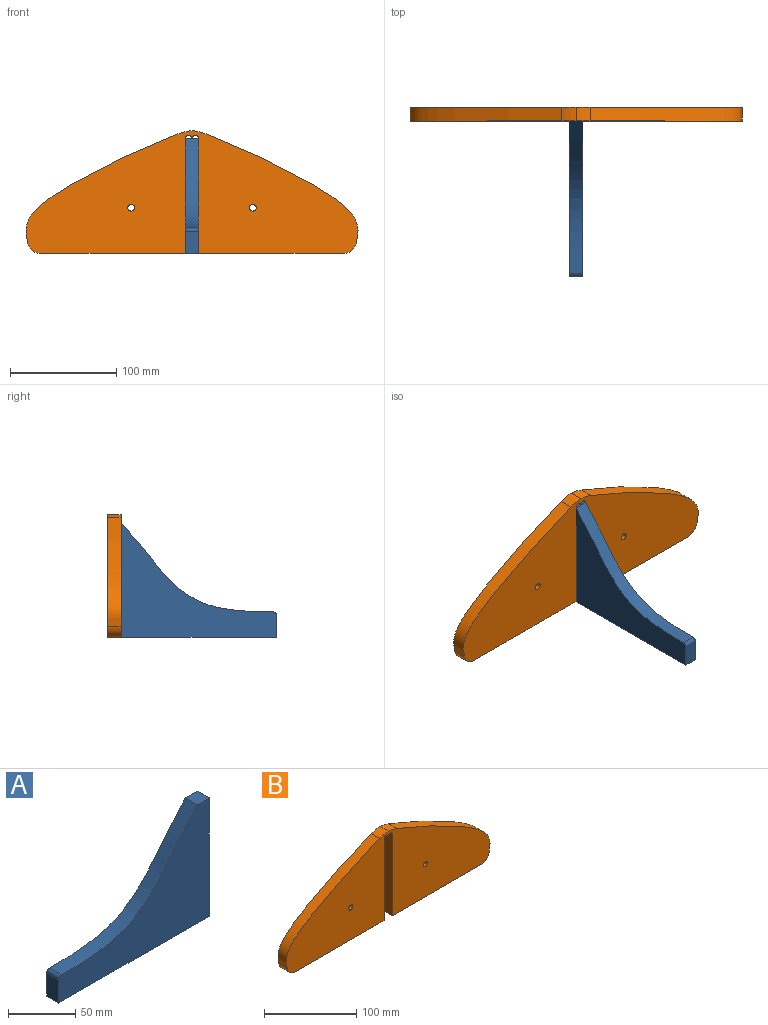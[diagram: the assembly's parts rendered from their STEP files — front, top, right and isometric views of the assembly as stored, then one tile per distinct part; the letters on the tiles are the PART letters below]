
ASSEMBLY  parts=2 mates=1
PART A: 8 faces, bbox 158.8x12.7x108 mm
  f0: plane 12.7x12.7mm, normal (0,0,1), area 161.3mm2, adj f1,f5,f6,f7
  f1: extruded ~142.95x83.92mm, area 2233.3mm2, adj f0,f2,f6,f7
  f2: cylinder r=3.17mm len=12.7mm, axis (0,1,0), area 62.4mm2, adj f1,f3,f6,f7
  f3: plane 20.86x12.7mm, normal (-1,0,0), area 264.9mm2, adj f2,f4,f6,f7
  f4: plane 158.75x12.7mm, normal (0,0,-1), area 2016.1mm2, adj f3,f5,f6,f7
  f5: plane 107.95x12.7mm, normal (1,0,0), area 1371mm2, adj f0,f4,f6,f7
  f6: plane 158.75x107.95mm, normal (0,-1,0), area 8181.7mm2, adj f0,f1,f2,f3,f4,f5
  f7: plane 158.75x107.95mm, normal (0,1,0), area 8181.7mm2, adj f0,f1,f2,f3,f4,f5
PART B: 16 faces, bbox 319.9x12.7x115.5 mm
  f0: plane 107.95x12.7mm, normal (1,0,0), area 1371mm2, adj f1,f12,f14,f15
  f1: cylinder r=3.17mm len=12.7mm, axis (0,1,0), area 126.7mm2, adj f0,f2,f14,f15
  f2: cylinder r=3.17mm len=12.7mm, axis (0,1,0), area 126.7mm2, adj f1,f3,f14,f15
  f3: plane 107.95x12.7mm, normal (-1,0,0), area 1371mm2, adj f2,f4,f14,f15
  f4: plane 135.65x12.7mm, normal (0,0,-1), area 1722.8mm2, adj f3,f5,f14,f15
  f5: cylinder r=12.7mm len=12.7mm, axis (0,1,0), area 222.9mm2, adj f4,f6,f14,f15
  f6: extruded ~142.72x102mm, area 2355.1mm2, adj f5,f7,f14,f15
  f7: cylinder r=50.8mm len=13.26mm, axis (0,1,0), area 173.7mm2, adj f6,f8,f14,f15
  f8: cylinder r=50.8mm len=13.26mm, axis (0,1,0), area 173.7mm2, adj f7,f9,f14,f15
  f9: extruded ~142.72x102mm, area 2355.1mm2, adj f8,f10,f14,f15
  f10: cylinder r=12.7mm len=12.7mm, axis (0,1,0), area 222.9mm2, adj f9,f12,f14,f15
  f11: cylinder r=3.17mm len=12.7mm, axis (0,1,0), area 253.4mm2, adj f14,f15
  f12: plane 135.65x12.7mm, normal (0,0,-1), area 1722.8mm2, adj f0,f10,f14,f15
  f13: cylinder r=3.17mm len=12.7mm, axis (0,1,0), area 253.4mm2, adj f14,f15
  f14: plane 319.94x115.48mm, normal (0,-1,0), area 23740.6mm2, adj f0,f1,f2,f3,f4,f5,f6,f7
  f15: plane 319.94x115.48mm, normal (0,1,0), area 23740.6mm2, adj f0,f1,f2,f3,f4,f5,f6,f7
PLACE A rot(axis=(0,0,1),90deg) t=(-148.18,-76.21,65.5)mm
PLACE B t=(-47.2,5.65,24.6)mm
MATE fastened A.f5 <-> B.f15  axis (0,1,0) through (-135.48,5.65,24.6)mm
